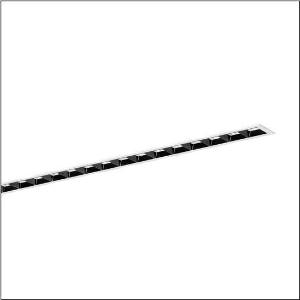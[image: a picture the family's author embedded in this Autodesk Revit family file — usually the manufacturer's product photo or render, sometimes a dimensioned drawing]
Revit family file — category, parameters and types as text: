
# Revit family: silica_21_51mx12dc3awb
name_source: partatom
category: Lighting Fixtures
units: mm (PartAtom-declared; Revit-internal decimal feet)

## family parameters
Cut with Voids When Loaded = No
Host = Face
Light Source = No
Part Type = Normal
Room Calculation Point = No
Round Connector Dimension = Use Diameter
Shared = No

## types (1)
- --- (1 x LED, 10800 lm, 69.2 W, 3000K)
    Apparent Load = 69 VA
    CIE Flux Codes = 86 100 100 100 100
    Color Rendering = 80
    Color Temperature = 3000K
    Default Elevation = 1800 mm
    Description = Silica 21, office luminaire, primary light control with darklight reflector, of PMMA, black, CAT 2 (L<= 3000cd/m²), light emission: direct distribution, primary light characteristic: symmetric, installation type: recessed, LED, rated luminous flux: 10.800lm, luminous efficacy: 156lm/W, light colour: 830, colour temperature: 3000K, control gear: DALI 2, with terminal, 3+2-pole, max. 2.5mm², mains connection: 220..240V, AC, 50/60Hz, rated input power: 69.2W, luminaire housing, of aluminium, traffic white (RAL 9016), length: 3.028mm, width: 79mm, height: 53mm, protection rating (complete): IP20, insulation class (complete): insulation class I (protective earthing), certification: CE, ENEC, VDE, permissible operating ambient temperature: 0..+35°C, standard: EN 50419, packaging unit: 1 piece
    Height = 0 mm  [stored 0 ft]
    Lamp = 1 x LED
    Lamp Light Flux = 10800 lm
    Lamp Power = 69.2 W
    Lamp count = 1
    Length = 3027 mm
    Luminous efficacy = 156 lm/W
    Manufacturer = Siteco
    ModVariant = No
    Model = 51MX12DC3AWB
    Mounting Place = Ceiling
    Mounting Type = Recessed
    Number of Poles = 1
    OnlyDefault = Yes
    Power Factor = 1
    Product Name = Silica 21
    Product group = office luminaire | ceiling recessed
    ProductGroupID = 400
    Protection Class = Protection class I
    Protection Degree = IP 20
    RLX_Detail_Level = 1
    RLX_Emergency_Light_Flux = 0 lm
    RLX_Emergency_Type = 0
    RLX_Emergency_Type_DB = No
    RlxData = <blob elided: 63029 chars, md5=3c9640b4>
    Socket = socket
    Standby Power = 0 W
    System Light Flux = 10800 lm
    System Power = 69 W
    Type Comments = factory setting: luminous flux: 100 % | dim-lin: 254 | 392 mA
    Type Image = l_1335880.jpg
    URL = http://relux.com
    VarID = @adj_126059
    Voltage = 0 V
    Weight = 0.00 kg
    Width = 79 mm

note: [stored X ft] marks values corroborated as IEEE doubles in the binary element streams (Revit-internal decimal feet)

## geometry (parser evidence)
native form markers: Blend x4, Sweep x11
no freeform markers — native parametric forms only
